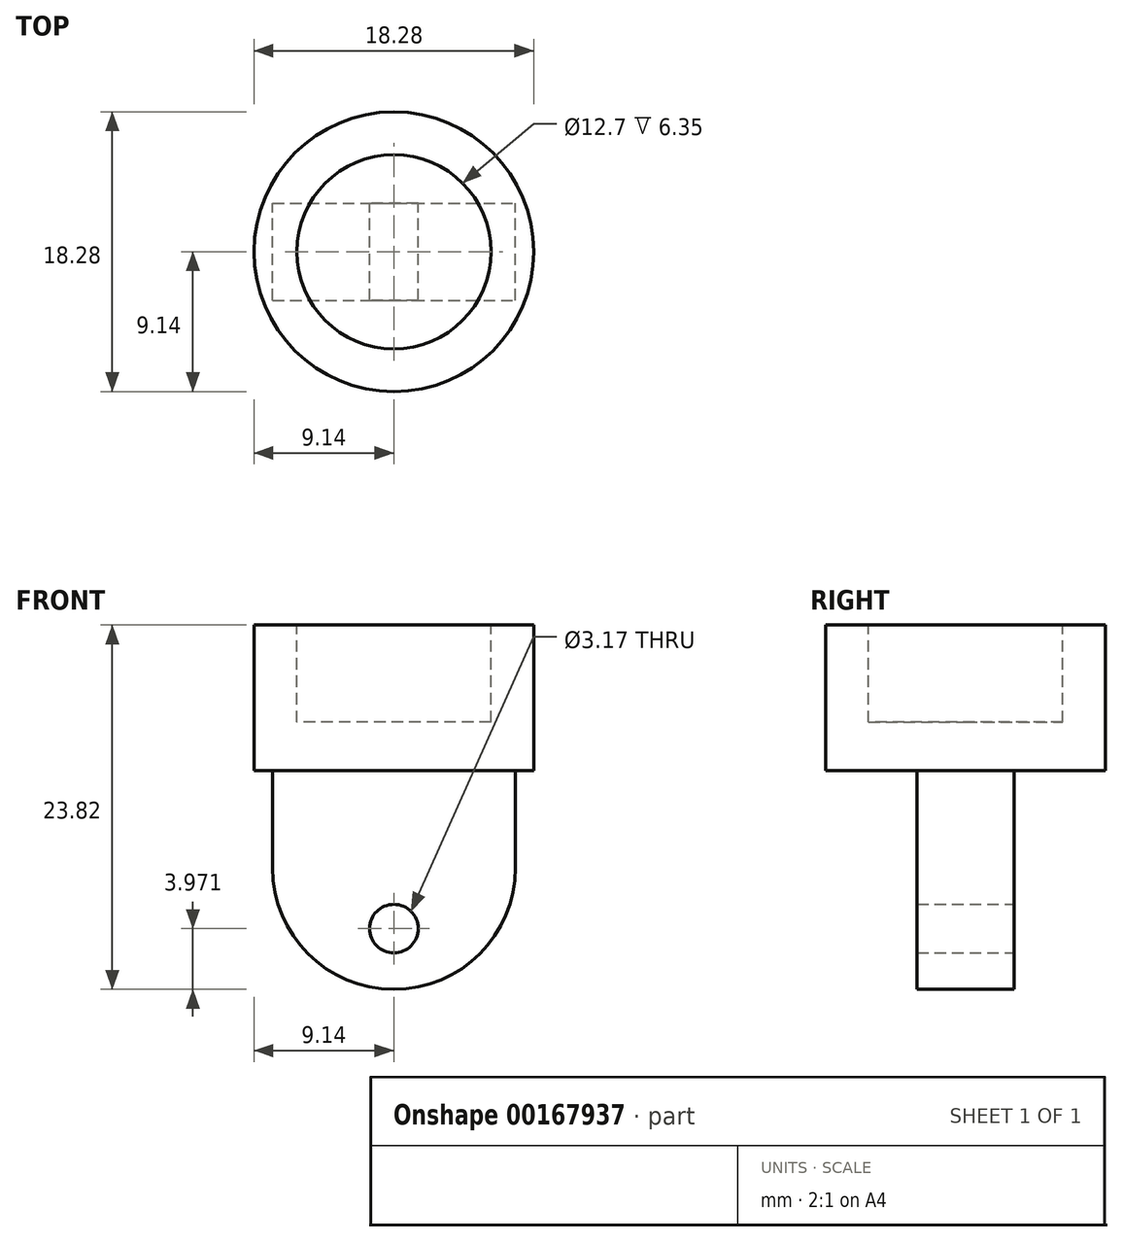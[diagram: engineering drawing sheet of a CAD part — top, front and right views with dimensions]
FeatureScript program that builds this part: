
annotation { "Feature Type Name" : "Feature", "Feature Type Description" : "" }
export const myFeature = defineFeature(function(context is Context, id is Id, definition is map)
    precondition{}
    {
        {
            var Q0;
            Q0=qCreatedBy(makeId("Top.planeOp"),FACE);
            var sketch = newSketch(context, id + "F0", { "sketchPlane" : qUnion([Q0])});
            skCircle(sketch, "E0", {"center": v(0, 0) * mm, "radius": 9.14 * mm});
            skSolve(sketch);
        }
        {
            var Q0;
            Q0 = qSketchRegion(id + "F0", true);
            extrude(context, id + "F1", {"entities" : qUnion([Q0]), "depth" : 9.52 * mm});
        }
        {
            var Q0;
            Q0=makeQuery(id+"F1.opExtrude","CAP_FACE",FACE,{"disambiguationData":[OSD([sQuery(id+"F0.wireOp",EDGE,"E0")])],"isStart":false});
            var sketch = newSketch(context, id + "F2", { "sketchPlane" : qUnion([Q0])});
            skCircle(sketch, "E1", {"center": v(0, 0) * mm, "radius": 6.35 * mm});
            skSolve(sketch);
        }
        {
            var Q0;
            Q0 = qSketchRegion(id + "F2", true);
            extrude(context, id + "F3", {"entities" : qUnion([Q0]), "operationType" : NewBodyOperationType.REMOVE, "oppositeDirection" : true, "depth" : 6.35 * mm});
        }
        {
            var Q0;
            Q0=makeQuery(id+"F1.opExtrude","CAP_FACE",FACE,{"disambiguationData":[OSD([sQuery(id+"F0.wireOp",EDGE,"E0")])],"isStart":true});
            var sketch = newSketch(context, id + "F4", { "sketchPlane" : qUnion([Q0])});
            skLineSegment(sketch, "E2.bottom", {"start": v(-7.94, 3.17) * mm, "end": v(7.94, 3.17) * mm});
            skLineSegment(sketch, "E2.top", {"start": v(-7.94, -3.18) * mm, "end": v(7.94, -3.18) * mm});
            skLineSegment(sketch, "E2.left", {"start": v(-7.94, 3.17) * mm, "end": v(-7.94, -3.18) * mm});
            skLineSegment(sketch, "E2.right", {"start": v(7.94, 3.17) * mm, "end": v(7.94, -3.18) * mm});
            skPoint(sketch, "E2.middle", {"position": v(0, 0) * mm});
            skSolve(sketch);
        }
        {
            var Q0;
            Q0=makeQuery(id+"F4.imprint","IMPRINT",FACE,{"disambiguationData":[TD([[makeQuery(id+"F4.imprint","IMPRINT",EDGE,{"derivedFrom":sQuery(id+"F4.wireOp",EDGE,"E2.bottom")}),-1.0]])]});
            extrude(context, id + "F5", {"entities" : qUnion([Q0]), "operationType" : NewBodyOperationType.ADD, "depth" : 6.35 * mm});
        }
        {
            var Q0;
            Q0=qCreatedBy(makeId("Front.planeOp"),FACE);
            var sketch = newSketch(context, id + "F6", { "sketchPlane" : qUnion([Q0])});
            skLineSegment(sketch, "E3.0", {"start": v(-7.94, -6.35) * mm, "end": v(7.94, -6.35) * mm});
            skArc(sketch, "E4", {"start": v(-7.94, -6.35) * mm, "mid": v(0, -14.29) * mm, "end": v(7.94, -6.35) * mm});
            skLineSegment(sketch, "E5", {"start": v(0, -6.35) * mm, "end": v(0, -14.29) * mm, "construction": true});
            skCircle(sketch, "E6", {"center": v(0, -10.32) * mm, "radius": 1.59 * mm});
            skSolve(sketch);
        }
        {
            var Q0;
            Q0 = qSketchRegion(id + "F6", true);
            extrude(context, id + "F7", {"entities" : qUnion([Q0]), "operationType" : NewBodyOperationType.ADD, "endBound" : BoundingType.SYMMETRIC, "depth" : 6.35 * mm});
        }
    });
